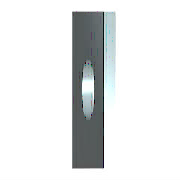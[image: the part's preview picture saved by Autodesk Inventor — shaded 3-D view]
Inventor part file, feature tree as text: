
AUTODESK INVENTOR PART (.ipt)
format: ipt  version: 2011 (Build 150239000, 239)  size: 98,816 bytes
history: native  units: mm (DEFAULTED — no unit token found)
features: other x1, plane x1
ambient origin geometry x7: Origin, YZ Plane, XY Plane, X Axis, Y Axis, Z Axis, Center Point
bodies: Solid1 (feature_tree), Body (feature_tree)
feature tree (2):
  other  "Work Axis1"
  plane  "Work Plane1"
